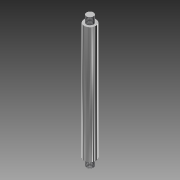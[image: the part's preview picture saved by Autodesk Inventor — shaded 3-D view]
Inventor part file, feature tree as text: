
AUTODESK INVENTOR PART (.ipt)
format: ipt  version: 2015 (Build 190159000, 159)  size: 82,432 bytes
history: native  units: mm
features: extrude x3, sketch x3, thread x2
ambient origin geometry x8: Origin, YZ Plane, XZ Plane, XY Plane, X Axis, Y Axis, Z Axis, Center Point
bodies: Solid1 (feature_tree)
feature tree (8):
  extrude  "Extrusion1"  Depth=50.0mm TaperAngle=0.0deg
  extrude  "Extrusion2"  Depth=3.0mm TaperAngle=0.0deg
  thread  "Thread1"  [1 undecoded]
  extrude  "Extrusion3"  Depth=3.0mm TaperAngle=0.0deg
  thread  "Thread2"  [1 undecoded]
  sketch  "Sketch1"  dims[d0=5.0mm d1=50.0mm d2=0.0mm]
  sketch  "Sketch2"  dims[d3=3.0mm d4=3.0mm d5=0.0mm d6=10.0mm d7=0.0mm]
  sketch  "Sketch3"  dims[d8=3.0mm d9=3.0mm d10=0.0mm d11=10.0mm d12=0.0mm]
note: 2 required parameter values undecoded (feature->parameter linkage not recoverable at this tier; creation-order binding heuristic only, values carry confidence <= 0.55)
